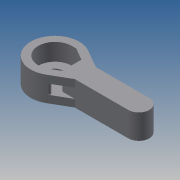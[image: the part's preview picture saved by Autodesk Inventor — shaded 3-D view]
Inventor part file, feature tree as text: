
AUTODESK INVENTOR PART (.ipt)
format: ipt  version: 2013 (Build 170138000, 138)  size: 357,376 bytes
history: native  units: mm
features: extrude x14, sketch x14, fillet x2, mirror x1, projected_geometry x1
ambient origin geometry x8: Origin, YZ Plane, XZ Plane, XY Plane, X Axis, Y Axis, Z Axis, Center Point
bodies: Solid1 (feature_tree)
feature tree (32):
  extrude  "Extrusion1"  Depth=112.5mm
  extrude  "Extrusion2"  Depth=65.0mm
  extrude  "Extrusion3"  Depth=45.0mm
  extrude  "Extrusion4"  Depth=23.0mm TaperAngle=0.0deg
  extrude  "Extrusion5"  Depth=13.0mm TaperAngle=0.0deg
  extrude  "Extrusion6"  Depth=13.0mm TaperAngle=0.0deg
  extrude  "Extrusion7"  Depth=2.5mm
  mirror  "Mirror1"
  fillet  "Fillet1"  Radius=22.0mm
  extrude  "Extrusion8"  Depth=15.0mm
  extrude  "Extrusion9"  Depth=3.5mm
  fillet  "Fillet2"  Radius=40.0mm
  extrude  "Extrusion10"  Depth=10.0mm TaperAngle=0.0deg
  extrude  "Extrusion11"  Depth=30.0mm
  extrude  "Extrusion12"  Depth=10.0mm TaperAngle=0.0deg
  extrude  "Extrusion13"  Depth=3.5mm
  extrude  "Extrusion14"  Depth=7.0mm
  sketch  "Sketch1"  dims[d0=28.0mm d2=112.5mm]
  sketch  "Sketch2"  dims[d3=33.0mm d4=0.0mm d5=65.0mm]
  sketch  "Sketch3"  dims[d7=33.0mm d8=0.0mm d10=45.0mm]
  sketch  "Sketch4"  dims[d12=23.0mm d13=0.0mm d14=23.0mm d15=0.0mm]
  sketch  "Sketch5"  dims[d16=60.0deg d17=13.0mm d18=0.0mm]
  projected_geometry  "Projected Loop1"
  sketch  "Sketch6"  dims[d19=10.0mm d20=13.0mm d21=0.0mm]
  sketch  "Sketch7"  dims[d22=13.0mm d23=0.0mm d24=2.5mm d25=22.0mm]
  sketch  "Sketch8"  dims[d27=7.0mm d28=0.0mm d29=15.0mm]
  sketch  "Sketch9"  dims[d31=7.0mm d32=0.0mm d33=3.5mm d34=40.0mm]
  sketch  "Sketch10"  dims[d35=12.0mm d36=10.0mm d37=0.0mm]
  sketch  "Sketch11"  dims[d38=8.0mm d39=30.0mm]
  sketch  "Sketch12"  dims[d40=45.0mm d41=10.0mm d42=0.0mm]
  sketch  "Sketch13"  dims[d43=8.0mm d45=3.5mm]
  sketch  "Sketch14"  dims[d47=5.0mm d48=7.0mm d49=10.0mm d50=0.0mm d51=6.0mm d53=3.0mm d54=0.0mm d55=5.5mm d56=4.0mm d57=0.0mm d59=8.0mm]
